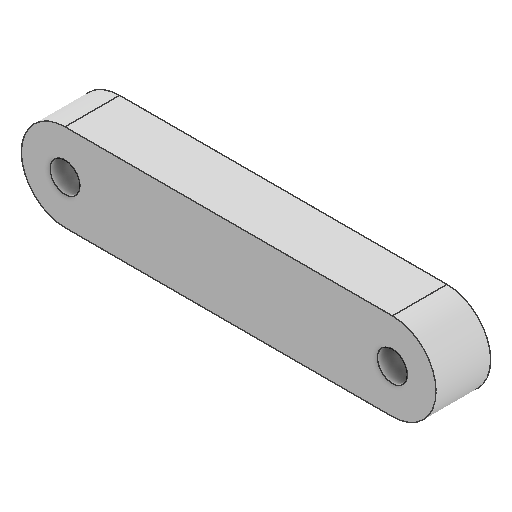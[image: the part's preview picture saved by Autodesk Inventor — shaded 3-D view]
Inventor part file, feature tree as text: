
AUTODESK INVENTOR PART (.ipt)
format: ipt  version: 2025 (Build 290162000, 162)  size: 95,744 bytes
history: native  units: mm
features: extrude x1, sketch x1
ambient origin geometry x8: Origin, YZ Plane, XZ Plane, XY Plane, X Axis, Y Axis, Z Axis, Center Point
bodies: Solid1 (feature_tree)
feature tree (2):
  extrude  "Extrusion1"  Depth=8.0mm
  sketch  "Sketch1"  dims[d0=60.0mm d1=8.0mm d2=5.5mm d3=10.0mm d4=0.0mm]
